# Revit family: Specialty_Equipment-CityScapes-NatureScreen
name_source: partatom
category: Specialty Equipment
units: mm (PartAtom-declared; Revit-internal decimal feet)

## family parameters
Classification Number = 23.40.10.24
Cut with Voids When Loaded = No
Enable Cutting in Views = No
Host = Face
Maintain Annotation Orientation = No
Part Type = Normal
Room Calculation Point = No
Round Connector Dimension = Use Diameter
Shared = No

## types (3) — shared parameters
Assembly Code = G2040
CD_Finish Frame = Metal-Nature_Screen-Aluminum_Frame
CD_Finish Graphics = Site-Nature_Screen-Foliage
CD_Height Max = 10' - 1 1/4"
CD_Height Min = 1' - 0"
CD_Microsite = https://www.caddetails.com
CD_Product Documentation Link = https://9415688.fs1.hubspotusercontent-na1.net
CD_Product Page URL = https://cityscapesinc.com
CD_Width Max = 5' - 1 1/2"
CD_Width Min = 1' - 0"
Default Elevation = 4' - 0"
Description = Wall Mounted Nature Screen
Manufacturer = CityScapes
Model = NatureScreen®
URL = https://cityscapesinc.com

## per-type parameters (varying)
| type | CD_C Bracket | CD_Double Mesh | CD_Finish | CD_Foliage | CD_Frame Thickness | CD_L Bracket | CD_Layer Offset | CD_Mesh Thickness | CD_Single Mesh | Type Comments |
| Single Mesh | No | No | Metal-Nature_Screen-Wire_Mesh-2"x2" | No | 0' - 1" | Yes | -0' - 0 1/16" | 0' - 0 1/32" | Yes | Single Mesh Trellis |
| Double Mesh | No | Yes | Metal-Nature_Screen-Wire_Mesh-2"x4" | No | 0' - 3" | Yes | 0' - 0 1/8" | 0' - 2 1/2" | No | Double Mesh Trellis |
| Graphic Mesh | Yes | Yes | Metal-Nature_Screen-Wire_Mesh-2"x2" | Yes | 0' - 3" | No | 0' - 0 1/8" | 0' - 2 1/2" | No | Graphic Mesh Trellis |

## geometry (parser evidence)
native form markers: Sweep x2
no freeform markers — native parametric forms only
